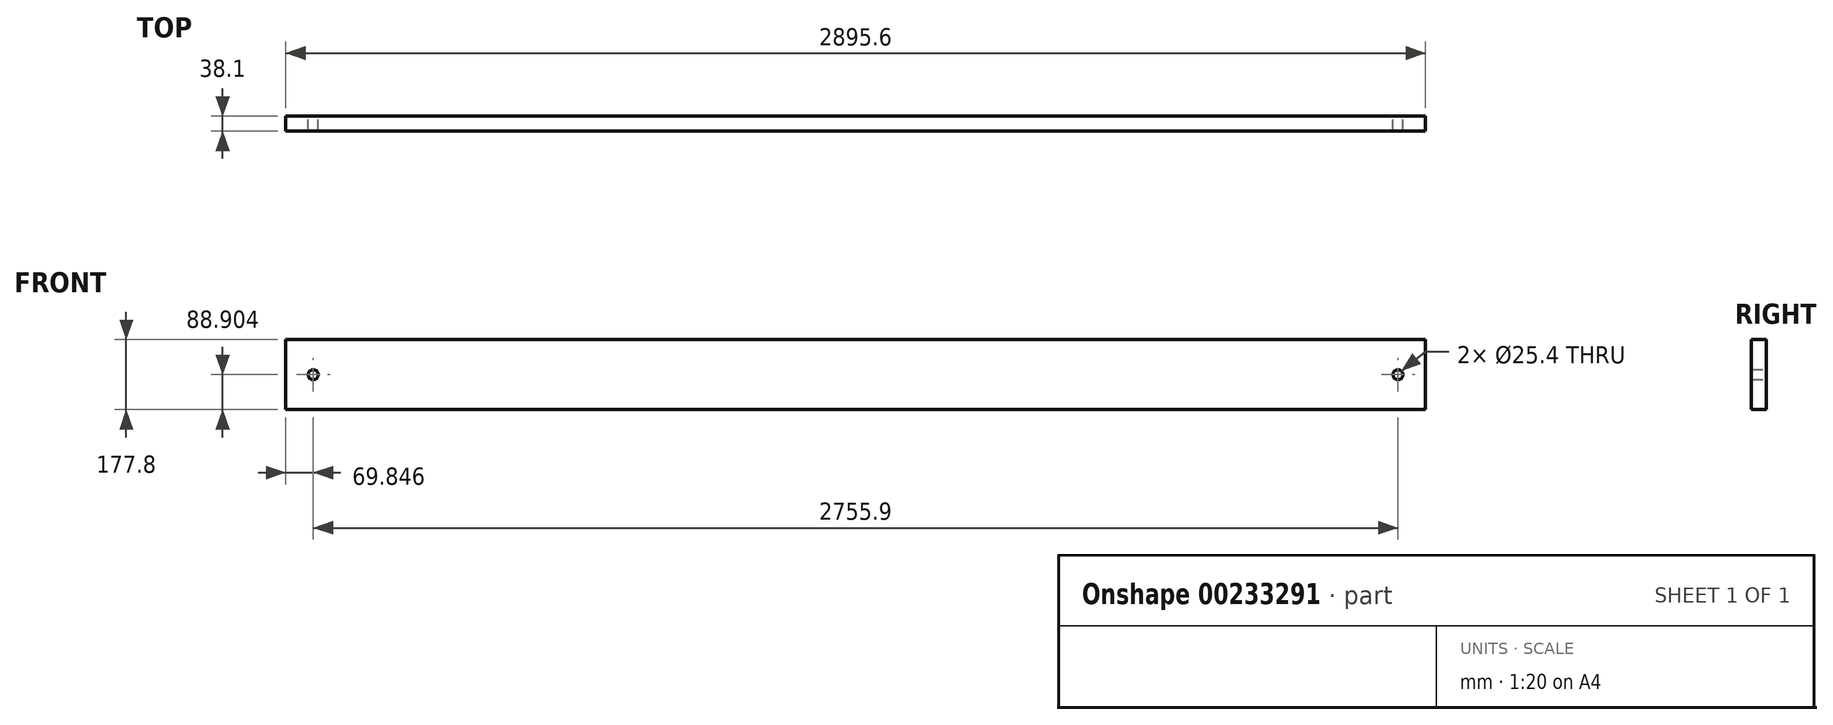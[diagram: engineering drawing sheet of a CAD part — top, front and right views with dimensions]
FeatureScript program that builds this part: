
annotation { "Feature Type Name" : "Feature", "Feature Type Description" : "" }
export const myFeature = defineFeature(function(context is Context, id is Id, definition is map)
    precondition{}
    {
        {
            var Q0;
            Q0=qCreatedBy(makeId("Front.planeOp"),FACE);
            var sketch = newSketch(context, id + "F0", { "sketchPlane" : qUnion([Q0])});
            skLineSegment(sketch, "E0.bottom", {"start": v(-1450.4, -211.78) * mm, "end": v(1445.2, -211.78) * mm});
            skLineSegment(sketch, "E0.top", {"start": v(-1450.4, -389.58) * mm, "end": v(1445.2, -389.58) * mm});
            skLineSegment(sketch, "E0.left", {"start": v(-1450.4, -211.78) * mm, "end": v(-1450.4, -389.58) * mm});
            skLineSegment(sketch, "E0.right", {"start": v(1445.2, -211.78) * mm, "end": v(1445.2, -389.58) * mm});
            skCircle(sketch, "E1", {"center": v(-1380.55, -300.68) * mm, "radius": 12.7 * mm});
            skPoint(sketch, "E1.centerSnap0", {"position": v(-1450.4, -300.68) * mm});
            skCircle(sketch, "E2", {"center": v(1375.35, -300.68) * mm, "radius": 12.7 * mm});
            skSolve(sketch);
        }
        {
            var Q0;
            Q0=makeQuery(id+"F0.imprint","IMPRINT",FACE,{"disambiguationData":[TD([[makeQuery(id+"F0.imprint","IMPRINT",EDGE,{"derivedFrom":sQuery(id+"F0.wireOp",EDGE,"E0.bottom")}),-1.0]])]});
            extrude(context, id + "F1", {"entities" : qUnion([Q0]), "depth" : 38.1 * mm});
        }
    });
